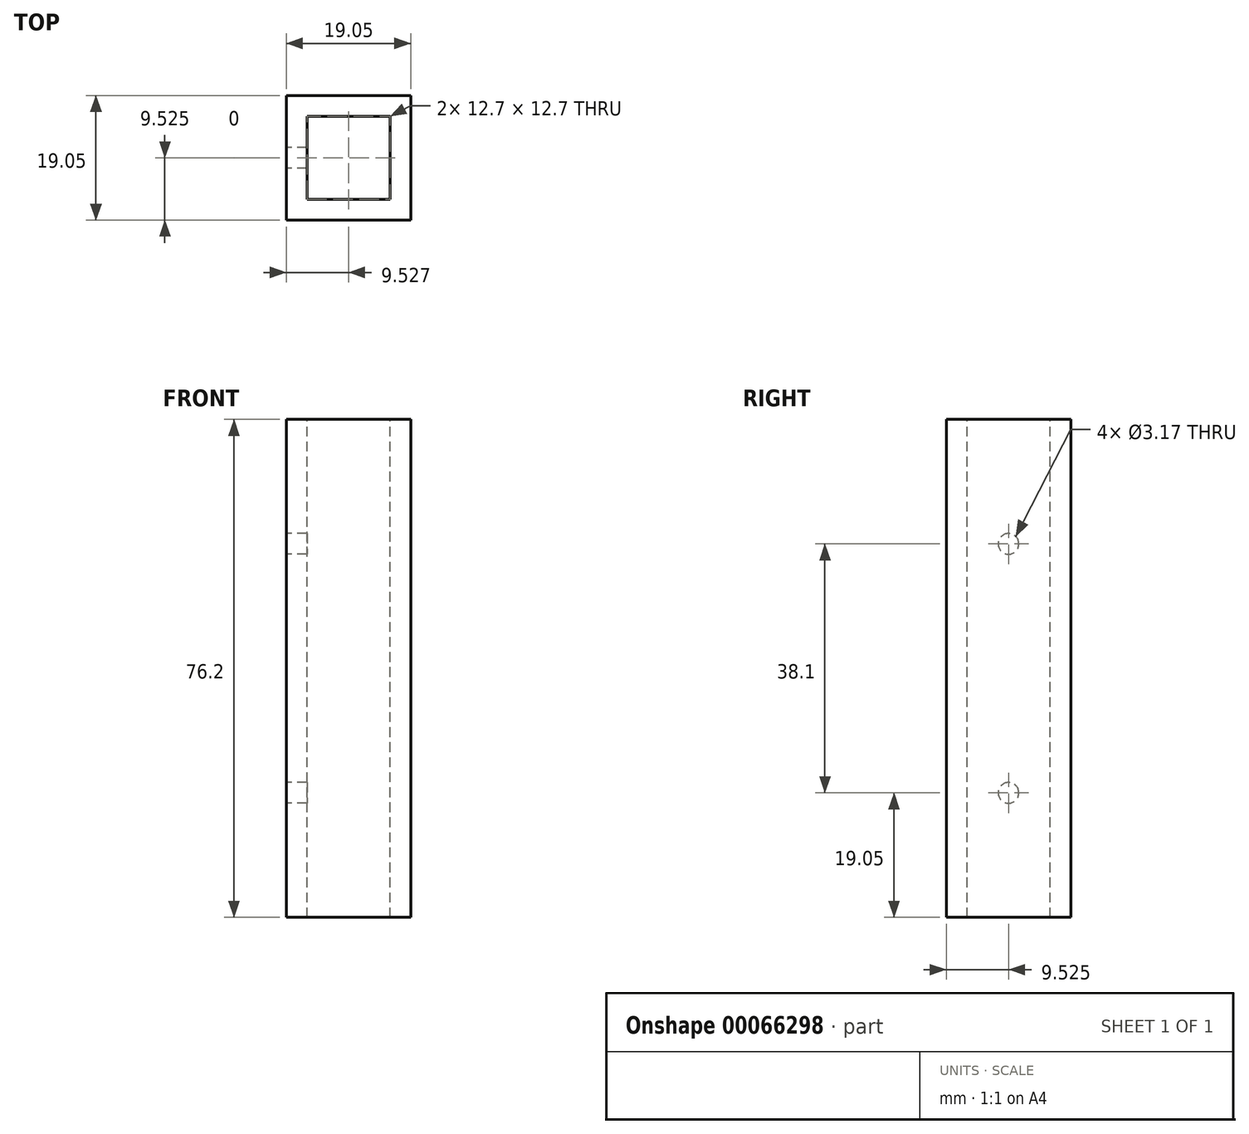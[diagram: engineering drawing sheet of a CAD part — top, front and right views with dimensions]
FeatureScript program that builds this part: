
annotation { "Feature Type Name" : "Feature", "Feature Type Description" : "" }
export const myFeature = defineFeature(function(context is Context, id is Id, definition is map)
    precondition{}
    {
        {
            var Q0;
            Q0=qCreatedBy(makeId("Front.planeOp"),FACE);
            var sketch = newSketch(context, id + "F0", { "sketchPlane" : qUnion([Q0])});
            skLineSegment(sketch, "E0.bottom", {"start": v(-95.33, 76.2) * mm, "end": v(-76.28, 76.2) * mm});
            skLineSegment(sketch, "E0.top", {"start": v(-95.33, 0) * mm, "end": v(-76.28, 0) * mm});
            skLineSegment(sketch, "E0.left", {"start": v(-95.33, 76.2) * mm, "end": v(-95.33, 0) * mm});
            skLineSegment(sketch, "E0.right", {"start": v(-76.28, 76.2) * mm, "end": v(-76.28, 0) * mm});
            skSolve(sketch);
        }
        {
            var Q0;
            Q0=makeQuery(id+"F0.imprint","IMPRINT",FACE,{"disambiguationData":[TD([[makeQuery(id+"F0.imprint","IMPRINT",EDGE,{"derivedFrom":sQuery(id+"F0.wireOp",EDGE,"E0.bottom")}),-1.0]])]});
            extrude(context, id + "F1", {"entities" : qUnion([Q0]), "depth" : 19.05 * mm});
        }
        {
            var Q0;
            Q0=makeQuery(id+"F1.opExtrude","SWEPT_FACE",FACE,{"disambiguationData":[OSD([sQuery(id+"F0.wireOp",EDGE,"E0.bottom")])]});
            var sketch = newSketch(context, id + "F2", { "sketchPlane" : qUnion([Q0])});
            skLineSegment(sketch, "E1.0", {"start": v(-95.33, 0) * mm, "end": v(-76.28, 0) * mm});
            skLineSegment(sketch, "E1.1", {"start": v(-95.33, -19.05) * mm, "end": v(-95.33, 0) * mm});
            skLineSegment(sketch, "E1.2", {"start": v(-95.33, -19.05) * mm, "end": v(-76.28, -19.05) * mm});
            skLineSegment(sketch, "E1.3", {"start": v(-76.28, -19.05) * mm, "end": v(-76.28, 0) * mm});
            skLineSegment(sketch, "E2.bottom", {"start": v(-92.15, -3.18) * mm, "end": v(-79.45, -3.18) * mm});
            skLineSegment(sketch, "E2.top", {"start": v(-92.15, -15.88) * mm, "end": v(-79.45, -15.88) * mm});
            skLineSegment(sketch, "E2.left", {"start": v(-92.15, -3.18) * mm, "end": v(-92.15, -15.88) * mm});
            skLineSegment(sketch, "E2.right", {"start": v(-79.45, -3.17) * mm, "end": v(-79.45, -15.88) * mm});
            skSolve(sketch);
        }
        {
            var Q0;
            Q0=makeQuery(id+"F2.imprint","IMPRINT",FACE,{"disambiguationData":[TD([[makeQuery(id+"F2.imprint","IMPRINT",EDGE,{"derivedFrom":sQuery(id+"F2.wireOp",EDGE,"E2.bottom")}),-1.0]])]});
            extrude(context, id + "F3", {"entities" : qUnion([Q0]), "operationType" : NewBodyOperationType.REMOVE, "endBound" : BoundingType.THROUGH_ALL, "oppositeDirection" : true, "depth" : 25.4 * mm});
        }
        {
            var Q0;
            Q0=makeQuery(id+"F1.opExtrude","SWEPT_FACE",FACE,{"disambiguationData":[OSD([sQuery(id+"F0.wireOp",EDGE,"E0.left")])]});
            var sketch = newSketch(context, id + "F4", { "sketchPlane" : qUnion([Q0])});
            skLineSegment(sketch, "E3.0", {"start": v(19.05, 0) * mm, "end": v(0, 0) * mm});
            skLineSegment(sketch, "E3.1", {"start": v(19.05, 76.2) * mm, "end": v(19.05, 0) * mm});
            skLineSegment(sketch, "E3.2", {"start": v(0, 76.2) * mm, "end": v(0, 0) * mm});
            skLineSegment(sketch, "E3.3", {"start": v(19.05, 76.2) * mm, "end": v(0, 76.2) * mm});
            skLineSegment(sketch, "E4", {"start": v(19.05, 0) * mm, "end": v(0, 76.2) * mm, "construction": true});
            skLineSegment(sketch, "E5", {"start": v(19.05, 76.2) * mm, "end": v(0, 0) * mm, "construction": true});
            skLineSegment(sketch, "E6", {"start": v(0, 38.1) * mm, "end": v(19.05, 38.1) * mm, "construction": true});
            skLineSegment(sketch, "E7", {"start": v(19.05, 38.1) * mm, "end": v(0, 0) * mm, "construction": true});
            skLineSegment(sketch, "E8", {"start": v(19.05, 0) * mm, "end": v(0, 38.1) * mm, "construction": true});
            skLineSegment(sketch, "E9", {"start": v(0, 38.1) * mm, "end": v(19.05, 76.2) * mm, "construction": true});
            skLineSegment(sketch, "E10", {"start": v(19.05, 38.1) * mm, "end": v(0, 76.2) * mm, "construction": true});
            skCircle(sketch, "E11", {"center": v(9.53, 19.05) * mm, "radius": 1.59 * mm});
            skCircle(sketch, "E12", {"center": v(9.52, 57.15) * mm, "radius": 1.59 * mm});
            skSolve(sketch);
        }
        {
            var Q0;
            Q0=makeQuery(id+"F4.imprint","IMPRINT",FACE,{"disambiguationData":[TD([[makeQuery(id+"F4.imprint","IMPRINT",EDGE,{"derivedFrom":sQuery(id+"F4.wireOp",EDGE,"E12")}),1.0]])]});
            var Q1;
            Q1=makeQuery(id+"F4.imprint","IMPRINT",FACE,{"disambiguationData":[TD([[makeQuery(id+"F4.imprint","IMPRINT",EDGE,{"derivedFrom":sQuery(id+"F4.wireOp",EDGE,"E11")}),1.0]])]});
            extrude(context, id + "F5", {"entities" : qUnion([Q0, Q1]), "operationType" : NewBodyOperationType.REMOVE, "oppositeDirection" : true, "depth" : 3.17 * mm});
        }
    });
